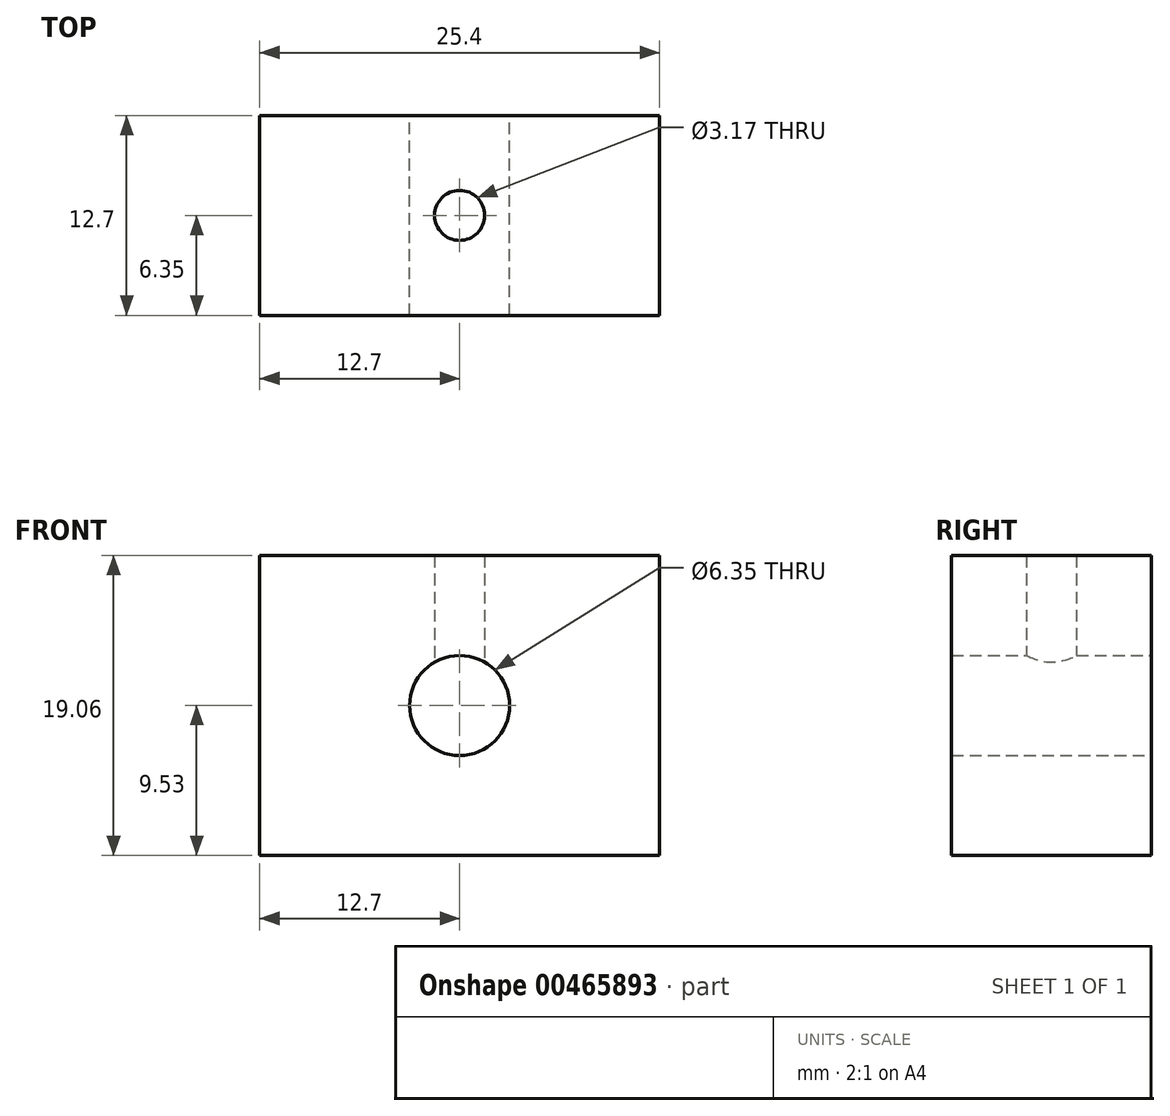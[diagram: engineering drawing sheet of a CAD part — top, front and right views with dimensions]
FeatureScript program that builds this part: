
annotation { "Feature Type Name" : "Feature", "Feature Type Description" : "" }
export const myFeature = defineFeature(function(context is Context, id is Id, definition is map)
    precondition{}
    {
        {
            var Q0;
            Q0=qCreatedBy(makeId("Front.planeOp"),FACE);
            var sketch = newSketch(context, id + "F0", { "sketchPlane" : qUnion([Q0])});
            skLineSegment(sketch, "E0.bottom", {"start": v(-12.7, 9.53) * mm, "end": v(12.7, 9.53) * mm});
            skLineSegment(sketch, "E0.top", {"start": v(-12.7, -9.53) * mm, "end": v(12.7, -9.53) * mm});
            skLineSegment(sketch, "E0.left", {"start": v(-12.7, 9.53) * mm, "end": v(-12.7, -9.53) * mm});
            skLineSegment(sketch, "E0.right", {"start": v(12.7, 9.53) * mm, "end": v(12.7, -9.52) * mm});
            skPoint(sketch, "E0.middle", {"position": v(0, 0) * mm});
            skCircle(sketch, "E1", {"center": v(0, 0) * mm, "radius": 3.18 * mm});
            skSolve(sketch);
        }
        {
            var Q0;
            Q0=makeQuery(id+"F0.imprint","IMPRINT",FACE,{"disambiguationData":[TD([[makeQuery(id+"F0.imprint","IMPRINT",EDGE,{"derivedFrom":sQuery(id+"F0.wireOp",EDGE,"E0.bottom")}),-1.0]])]});
            extrude(context, id + "F1", {"entities" : qUnion([Q0]), "endBound" : BoundingType.SYMMETRIC, "depth" : 12.7 * mm});
        }
        {
            var Q0;
            Q0=qCreatedBy(makeId("Top.planeOp"),FACE);
            var sketch = newSketch(context, id + "F2", { "sketchPlane" : qUnion([Q0])});
            skCircle(sketch, "E2", {"center": v(0, 0) * mm, "radius": 1.59 * mm});
            skSolve(sketch);
        }
        {
            var Q0;
            Q0=makeQuery(id+"F2.imprint","IMPRINT",FACE,{"disambiguationData":[TD([[makeQuery(id+"F2.imprint","IMPRINT",EDGE,{"derivedFrom":sQuery(id+"F2.wireOp",EDGE,"E2")}),1.0]])]});
            extrude(context, id + "F3", {"entities" : qUnion([Q0]), "operationType" : NewBodyOperationType.REMOVE, "oppositeDirection" : true, "depth" : -25.4 * mm});
        }
    });
